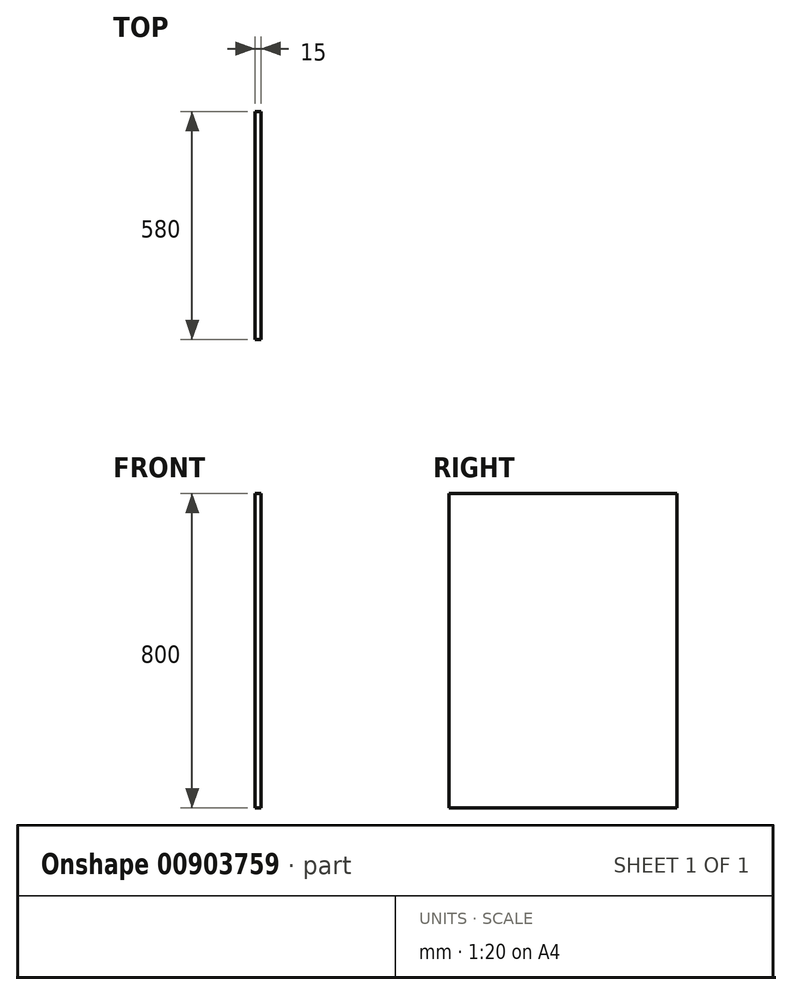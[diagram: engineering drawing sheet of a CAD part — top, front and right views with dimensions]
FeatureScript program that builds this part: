
annotation { "Feature Type Name" : "Feature", "Feature Type Description" : "" }
export const myFeature = defineFeature(function(context is Context, id is Id, definition is map)
    precondition{}
    {
        {
            var Q0;
            Q0=qCreatedBy(makeId("Right.planeOp"),FACE);
            var sketch = newSketch(context, id + "F0", { "sketchPlane" : qUnion([Q0])});
            skLineSegment(sketch, "E0.bottom", {"start": v(-290, 400) * mm, "end": v(290, 400) * mm});
            skLineSegment(sketch, "E0.top", {"start": v(-290, -400) * mm, "end": v(290, -400) * mm});
            skLineSegment(sketch, "E0.left", {"start": v(-290, 400) * mm, "end": v(-290, -400) * mm});
            skLineSegment(sketch, "E0.right", {"start": v(290, 400) * mm, "end": v(290, -400) * mm});
            skSolve(sketch);
        }
        {
            var Q0;
            Q0=makeQuery(id+"F0.imprint","IMPRINT",FACE,{"disambiguationData":[TD([[makeQuery(id+"F0.imprint","IMPRINT",EDGE,{"derivedFrom":sQuery(id+"F0.wireOp",EDGE,"E0.bottom")}),-1.0]])]});
            extrude(context, id + "F1", {"entities" : qUnion([Q0]), "oppositeDirection" : true, "depth" : 15 * mm, "offsetDistance" : 25 * mm});
        }
    });
